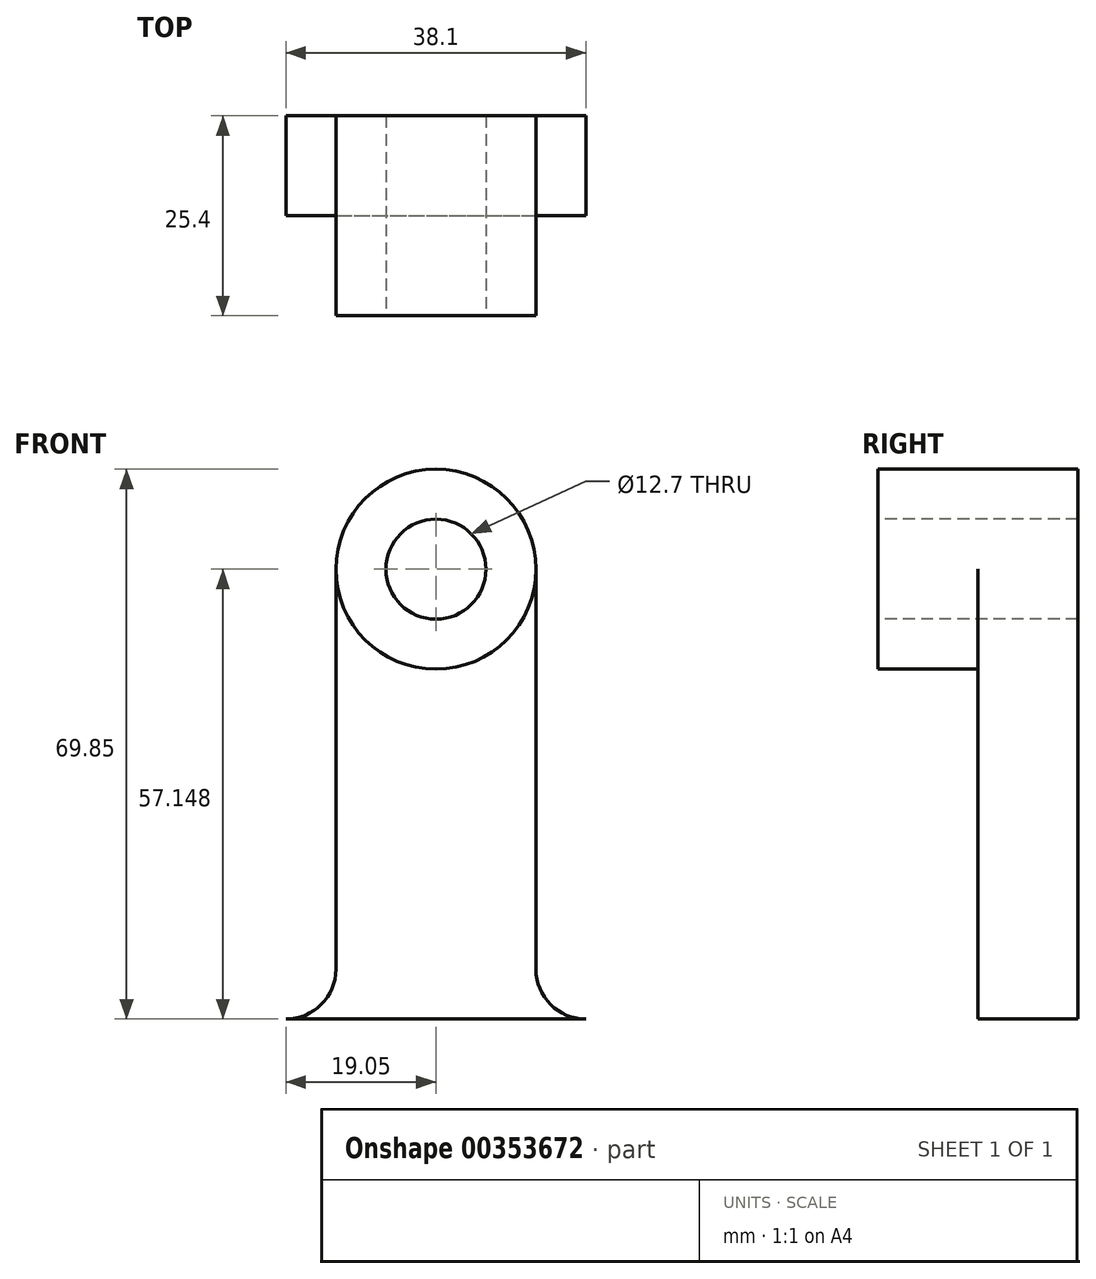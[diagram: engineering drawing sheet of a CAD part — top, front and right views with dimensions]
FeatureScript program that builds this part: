
annotation { "Feature Type Name" : "Feature", "Feature Type Description" : "" }
export const myFeature = defineFeature(function(context is Context, id is Id, definition is map)
    precondition{}
    {
        {
            var Q0;
            Q0=qCreatedBy(makeId("Front.planeOp"),FACE);
            var sketch = newSketch(context, id + "F0", { "sketchPlane" : qUnion([Q0])});
            skLineSegment(sketch, "E0", {"start": v(-44.26, 39.37) * mm, "end": v(-44.26, -30.48) * mm});
            skLineSegment(sketch, "E1", {"start": v(-44.26, -30.48) * mm, "end": v(6.54, -30.48) * mm});
            skLineSegment(sketch, "E2", {"start": v(6.54, -30.48) * mm, "end": v(6.54, 39.37) * mm});
            skLineSegment(sketch, "E3", {"start": v(6.54, 39.37) * mm, "end": v(-44.26, 39.37) * mm});
            skSolve(sketch);
        }
        {
            var Q0;
            Q0 = qSketchRegion(id + "F0", true);
            extrude(context, id + "F1", {"entities" : qUnion([Q0]), "depth" : 12.7 * mm});
        }
        {
            var Q0;
            Q0=makeQuery(id+"F1.opExtrude","CAP_FACE",FACE,{"disambiguationData":[OSD([sQuery(id+"F0.wireOp",EDGE,"E0"),sQuery(id+"F0.wireOp",EDGE,"E1"),sQuery(id+"F0.wireOp",EDGE,"E2"),sQuery(id+"F0.wireOp",EDGE,"E3")])],"isStart":false});
            var sketch = newSketch(context, id + "F2", { "sketchPlane" : qUnion([Q0])});
            skCircle(sketch, "E4", {"center": v(-18.86, 26.67) * mm, "radius": 6.35 * mm});
            skCircle(sketch, "E5", {"center": v(-18.86, 26.67) * mm, "radius": 12.7 * mm});
            skLineSegment(sketch, "E6", {"start": v(-31.56, 26.67) * mm, "end": v(-31.56, -24.13) * mm});
            skLineSegment(sketch, "E7", {"start": v(-37.9, -30.48) * mm, "end": v(-44.26, -30.48) * mm});
            skPoint(sketch, "E8.visualSharp", {"position": v(-31.56, -30.48) * mm});
            skArc(sketch, "E8.filletArc", {"start": v(-37.9, -30.48) * mm, "mid": v(-33.42, -28.62) * mm, "end": v(-31.56, -24.13) * mm});
            skLineSegment(sketch, "E9", {"start": v(-6.16, 26.67) * mm, "end": v(-6.16, -24.13) * mm});
            skLineSegment(sketch, "E10", {"start": v(0.2, -30.48) * mm, "end": v(6.54, -30.48) * mm});
            skPoint(sketch, "E11.visualSharp", {"position": v(-6.16, -30.48) * mm});
            skArc(sketch, "E11.filletArc", {"start": v(-6.16, -24.13) * mm, "mid": v(-4.3, -28.62) * mm, "end": v(0.2, -30.48) * mm});
            skSolve(sketch);
        }
        {
            var Q0;
            {var subQ0=sQuery(id+"F2.wireOp",EDGE,"E6");Q0=makeQuery(id+"F2.imprint","IMPRINT",FACE,{"disambiguationData":[TD([[makeQuery(id+"F2.imprint","IMPRINT",EDGE,{"derivedFrom":subQ0}),-1.0]])]});}
            var Q1;
            Q1=makeQuery(id+"F2.imprint","IMPRINT",FACE,{"disambiguationData":[TD([[makeQuery(id+"F2.imprint","IMPRINT",EDGE,{"derivedFrom":sQuery(id+"F2.wireOp",EDGE,"E4")}),1.0]])]});
            var Q2;
            {var subQ0=sQuery(id+"F2.wireOp",EDGE,"E9");Q2=makeQuery(id+"F2.imprint","IMPRINT",FACE,{"disambiguationData":[TD([[makeQuery(id+"F2.imprint","IMPRINT",EDGE,{"derivedFrom":subQ0}),1.0]])]});}
            extrude(context, id + "F3", {"entities" : qUnion([Q0, Q1, Q2]), "operationType" : NewBodyOperationType.REMOVE, "oppositeDirection" : true, "depth" : 31.75 * mm});
        }
        {
            var Q0;
            Q0 = qSketchRegion(id + "F2", true);
            extrude(context, id + "F4", {"entities" : qUnion([Q0]), "operationType" : NewBodyOperationType.ADD, "depth" : 12.7 * mm});
        }
    });
